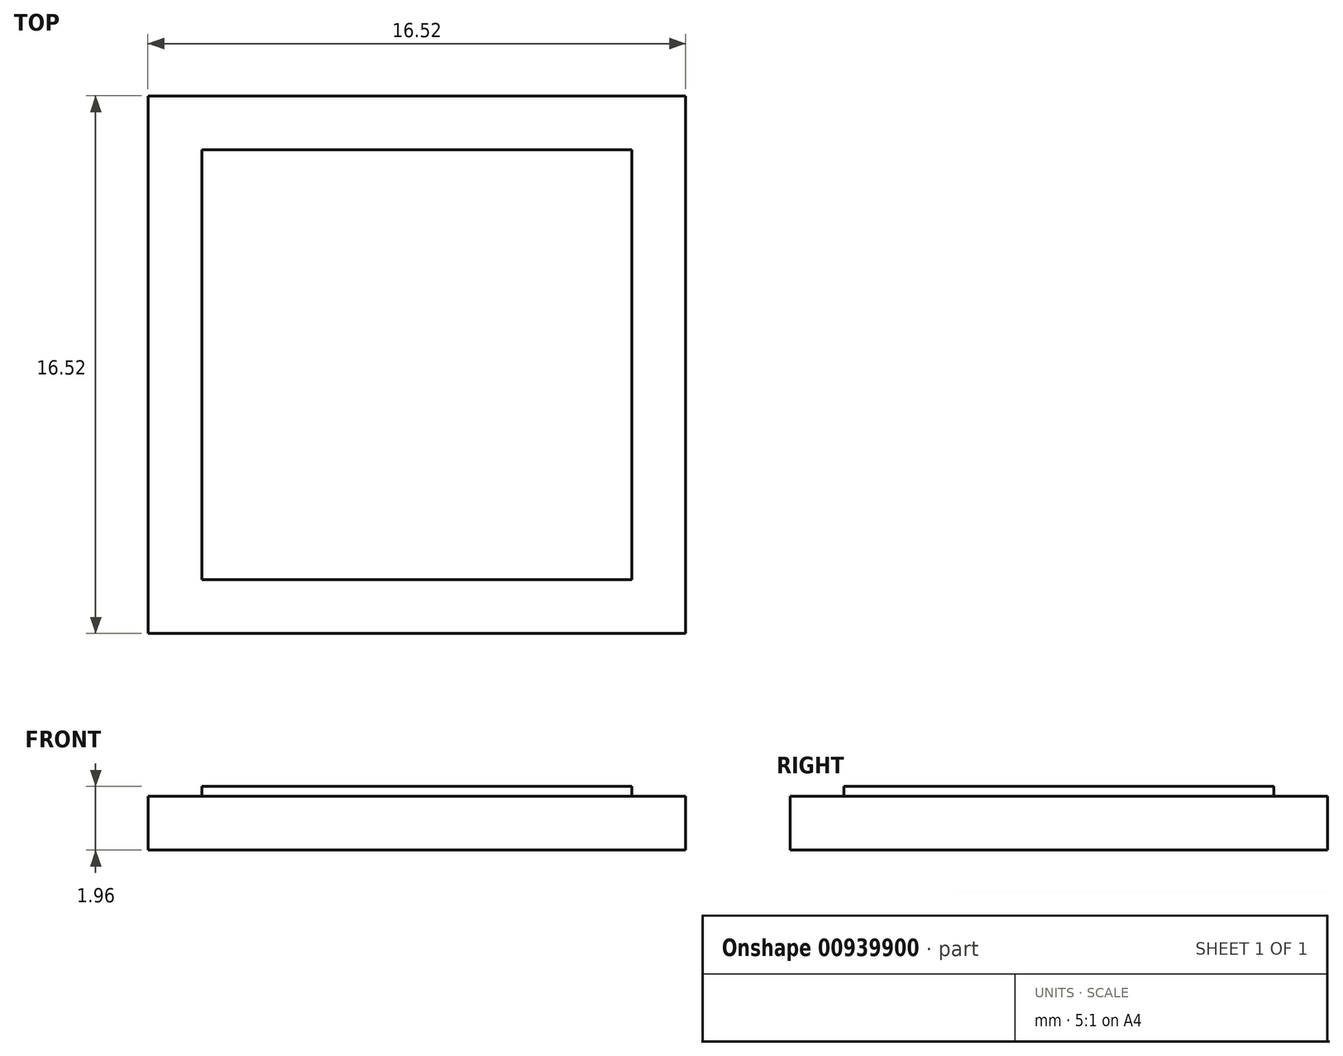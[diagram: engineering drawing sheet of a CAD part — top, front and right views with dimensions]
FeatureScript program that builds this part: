
annotation { "Feature Type Name" : "Feature", "Feature Type Description" : "" }
export const myFeature = defineFeature(function(context is Context, id is Id, definition is map)
    precondition{}
    {
        {
            var Q0;
            Q0=qCreatedBy(makeId("Top.planeOp"),FACE);
            var sketch = newSketch(context, id + "F0", { "sketchPlane" : qUnion([Q0])});
            skLineSegment(sketch, "E0.bottom", {"start": v(8.26, -8.26) * mm, "end": v(-8.26, -8.26) * mm});
            skLineSegment(sketch, "E0.top", {"start": v(8.26, 8.26) * mm, "end": v(-8.26, 8.26) * mm});
            skLineSegment(sketch, "E0.left", {"start": v(8.26, -8.26) * mm, "end": v(8.26, 8.26) * mm});
            skLineSegment(sketch, "E0.right", {"start": v(-8.26, -8.26) * mm, "end": v(-8.26, 8.26) * mm});
            skPoint(sketch, "E0.middle", {"position": v(0, 0) * mm});
            skLineSegment(sketch, "E1.bottom", {"start": v(6.6, -6.6) * mm, "end": v(-6.6, -6.6) * mm});
            skLineSegment(sketch, "E1.top", {"start": v(6.6, 6.6) * mm, "end": v(-6.6, 6.6) * mm});
            skLineSegment(sketch, "E1.left", {"start": v(6.6, -6.6) * mm, "end": v(6.6, 6.6) * mm});
            skLineSegment(sketch, "E1.right", {"start": v(-6.6, -6.6) * mm, "end": v(-6.6, 6.6) * mm});
            skLineSegment(sketch, "E2.bottom", {"start": v(5, -5) * mm, "end": v(-5, -5) * mm});
            skLineSegment(sketch, "E2.top", {"start": v(5, 5) * mm, "end": v(-5, 5) * mm});
            skLineSegment(sketch, "E2.left", {"start": v(5, -5) * mm, "end": v(5, 5) * mm});
            skLineSegment(sketch, "E2.right", {"start": v(-5, -5) * mm, "end": v(-5, 5) * mm});
            skSolve(sketch);
        }
        {
            var Q0;
            Q0=makeQuery(id+"F0.imprint","IMPRINT",FACE,{"disambiguationData":[TD([[makeQuery(id+"F0.imprint","IMPRINT",EDGE,{"derivedFrom":sQuery(id+"F0.wireOp",EDGE,"E0.bottom")}),-1.0]])]});
            extrude(context, id + "F1", {"entities" : qUnion([Q0]), "depth" : 1.65 * mm, "offsetDistance" : 25 * mm});
        }
        {
            var Q0;
            Q0 = qSketchRegion(id + "F0", true);
            var Q1;
            Q1=makeQuery(id+"F0.imprint","IMPRINT",FACE,{"disambiguationData":[TD([[makeQuery(id+"F0.imprint","IMPRINT",EDGE,{"derivedFrom":sQuery(id+"F0.wireOp",EDGE,"E1.bottom")}),-1.0]])]});
            var Q2;
            Q2=makeQuery(id+"F0.imprint","IMPRINT",FACE,{"disambiguationData":[TD([[makeQuery(id+"F0.imprint","IMPRINT",EDGE,{"derivedFrom":sQuery(id+"F0.wireOp",EDGE,"E2.bottom")}),-1.0]])]});
            extrude(context, id + "F2", {"entities" : qUnion([Q0, Q1, Q2]), "operationType" : NewBodyOperationType.ADD, "depth" : 0.56 * mm, "offsetDistance" : 25 * mm});
        }
        {
            var Q0;
            Q0=makeQuery(id+"F2.opExtrude","CAP_FACE",FACE,{"disambiguationData":[OSD([sQuery(id+"F0.wireOp",EDGE,"E0.bottom"),sQuery(id+"F0.wireOp",EDGE,"E0.top"),sQuery(id+"F0.wireOp",EDGE,"E0.left"),sQuery(id+"F0.wireOp",EDGE,"E0.right")])],"isStart":false});
            extrude(context, id + "F3", {"entities" : qUnion([Q0]), "operationType" : NewBodyOperationType.ADD, "depth" : 1.4 * mm, "offsetDistance" : 25 * mm});
        }
        {
            var Q0;
            Q0=makeQuery(id+"F0.imprint","IMPRINT",FACE,{"disambiguationData":[TD([[makeQuery(id+"F0.imprint","IMPRINT",EDGE,{"derivedFrom":sQuery(id+"F0.wireOp",EDGE,"E2.bottom")}),-1.0]])]});
            extrude(context, id + "F4", {"entities" : qUnion([Q0]), "operationType" : NewBodyOperationType.ADD, "depth" : 1.52 * mm, "offsetDistance" : 25 * mm});
        }
    });
